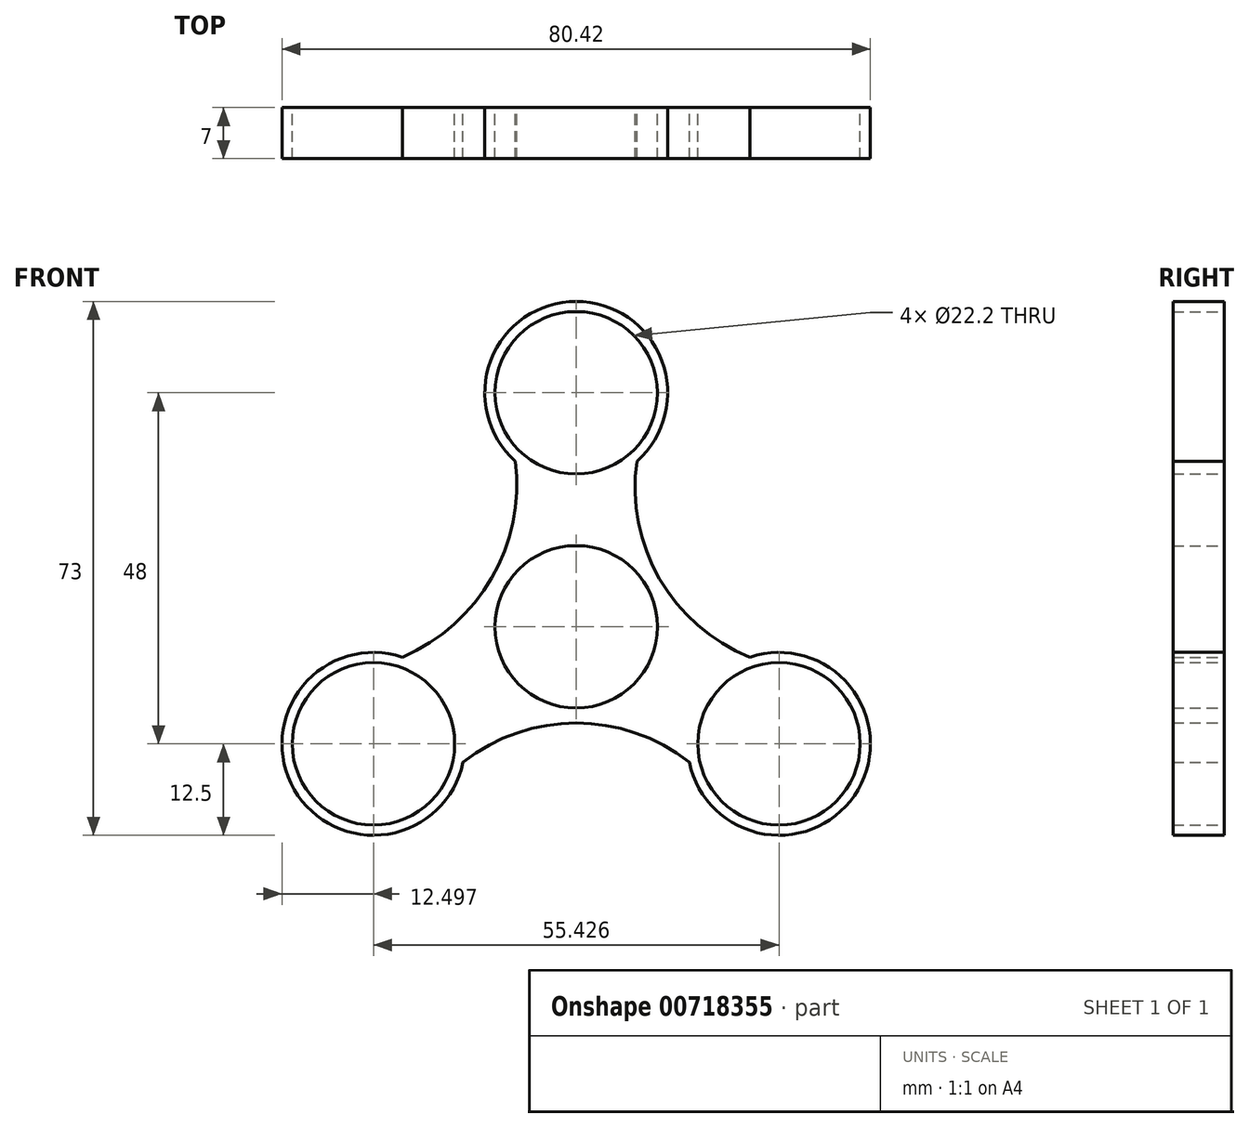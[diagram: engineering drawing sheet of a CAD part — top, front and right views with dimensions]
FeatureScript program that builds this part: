
annotation { "Feature Type Name" : "Feature", "Feature Type Description" : "" }
export const myFeature = defineFeature(function(context is Context, id is Id, definition is map)
    precondition{}
    {
        {
            var Q0;
            Q0=qCreatedBy(makeId("Front.planeOp"),FACE);
            var sketch = newSketch(context, id + "F0", { "sketchPlane" : qUnion([Q0])});
            skCircle(sketch, "E0", {"center": v(0, 0) * mm, "radius": 11.1 * mm});
            skCircle(sketch, "E1", {"center": v(0, 32) * mm, "radius": 11.1 * mm});
            skCircle(sketch, "E2.1.0", {"center": v(-27.71, -16) * mm, "radius": 11.1 * mm});
            skCircle(sketch, "E2.2.0", {"center": v(27.71, -16) * mm, "radius": 11.1 * mm});
            skArc(sketch, "E3", {"start": v(8.3, 22.65) * mm, "mid": v(0, 44.5) * mm, "end": v(-8.3, 22.65) * mm});
            skArc(sketch, "E4", {"start": v(-23.77, -4.14) * mm, "mid": v(-38.54, -22.25) * mm, "end": v(-15.47, -18.51) * mm});
            skArc(sketch, "E5", {"start": v(15.47, -18.51) * mm, "mid": v(38.54, -22.25) * mm, "end": v(23.77, -4.14) * mm});
            skArc(sketch, "E6", {"start": v(-23.77, -4.14) * mm, "mid": v(-23.6, -4.95) * mm, "end": v(-23.43, -5.76) * mm});
            skArc(sketch, "E7", {"start": v(-23.77, -4.14) * mm, "mid": v(-11.56, 6.67) * mm, "end": v(-8.3, 22.65) * mm});
            skArc(sketch, "E8", {"start": v(15.47, -18.51) * mm, "mid": v(0, -13.15) * mm, "end": v(-15.47, -18.51) * mm});
            skArc(sketch, "E9", {"start": v(8.3, 22.65) * mm, "mid": v(11.4, 6.58) * mm, "end": v(23.77, -4.14) * mm});
            skArc(sketch, "E10.trimOffspring", {"start": v(15.47, -18.51) * mm, "mid": v(16.1, -17.97) * mm, "end": v(16.7, -17.4) * mm});
            skArc(sketch, "E11.trimOffspring", {"start": v(8.3, 22.65) * mm, "mid": v(7.51, 22.92) * mm, "end": v(6.72, 23.17) * mm});
            skArc(sketch, "E12.trimOffspring", {"start": v(-6.72, 23.17) * mm, "mid": v(-7.51, 22.92) * mm, "end": v(-8.3, 22.65) * mm});
            skArc(sketch, "E13.trimOffspring", {"start": v(-16.7, -17.4) * mm, "mid": v(-16.1, -17.97) * mm, "end": v(-15.47, -18.51) * mm});
            skArc(sketch, "E14.trimOffspring", {"start": v(23.43, -5.76) * mm, "mid": v(23.6, -4.95) * mm, "end": v(23.77, -4.14) * mm});
            skSolve(sketch);
        }
        {
            var Q0;
            Q0=makeQuery(id+"F0.imprint","IMPRINT",FACE,{"disambiguationData":[TD([[makeQuery(id+"F0.imprint","IMPRINT",EDGE,{"derivedFrom":sQuery(id+"F0.wireOp",EDGE,"E3")}),1.0]])]});
            var Q1;
            Q1=makeQuery(id+"F0.imprint","IMPRINT",FACE,{"disambiguationData":[TD([[makeQuery(id+"F0.imprint","IMPRINT",EDGE,{"derivedFrom":sQuery(id+"F0.wireOp",EDGE,"E0")}),-1.0]])]});
            var Q2;
            Q2=makeQuery(id+"F0.imprint","IMPRINT",FACE,{"disambiguationData":[TD([[makeQuery(id+"F0.imprint","IMPRINT",EDGE,{"derivedFrom":sQuery(id+"F0.wireOp",EDGE,"E4")}),1.0]])]});
            var Q3;
            Q3=makeQuery(id+"F0.imprint","IMPRINT",FACE,{"disambiguationData":[TD([[makeQuery(id+"F0.imprint","IMPRINT",EDGE,{"derivedFrom":sQuery(id+"F0.wireOp",EDGE,"E5")}),1.0]])]});
            extrude(context, id + "F1", {"entities" : qUnion([Q0, Q1, Q2, Q3]), "depth" : 7 * mm, "offsetDistance" : 25 * mm});
        }
    });
